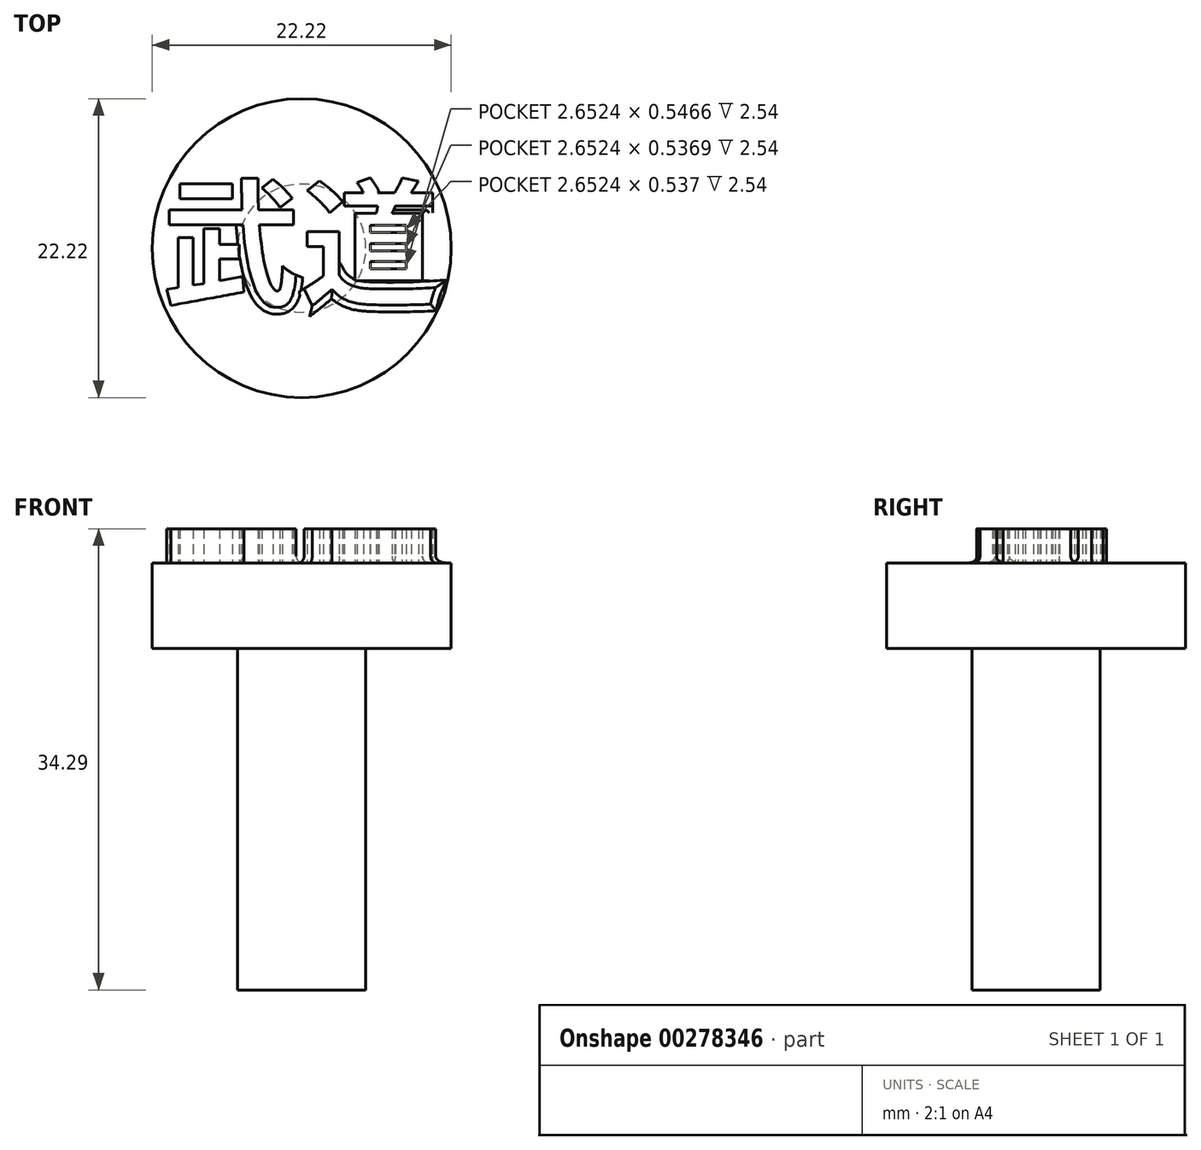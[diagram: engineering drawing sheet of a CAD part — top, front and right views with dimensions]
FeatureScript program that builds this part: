
annotation { "Feature Type Name" : "Feature", "Feature Type Description" : "" }
export const myFeature = defineFeature(function(context is Context, id is Id, definition is map)
    precondition{}
    {
        {
            var Q0;
            Q0=qCreatedBy(makeId("Top.planeOp"),FACE);
            var sketch = newSketch(context, id + "F0", { "sketchPlane" : qUnion([Q0])});
            skCircle(sketch, "E0", {"center": v(0, 0) * mm, "radius": 4.76 * mm});
            skSolve(sketch);
        }
        {
            var Q0;
            Q0 = qSketchRegion(id + "F0", true);
            extrude(context, id + "F1", {"entities" : qUnion([Q0]), "depth" : 25.4 * mm});
        }
        {
            var Q0;
            Q0=makeQuery(id+"F1.opExtrude","CAP_FACE",FACE,{"disambiguationData":[OSD([sQuery(id+"F0.wireOp",EDGE,"E0")])],"isStart":false});
            var sketch = newSketch(context, id + "F2", { "sketchPlane" : qUnion([Q0])});
            skCircle(sketch, "E1", {"center": v(0, 0) * mm, "radius": 11.11 * mm});
            skSolve(sketch);
        }
        {
            var Q0;
            Q0 = qSketchRegion(id + "F2", true);
            extrude(context, id + "F3", {"entities" : qUnion([Q0]), "operationType" : NewBodyOperationType.ADD, "depth" : 6.35 * mm});
        }
        {
            var Q0;
            Q0=makeQuery(id+"F3.opExtrude","CAP_FACE",FACE,{"disambiguationData":[OSD([sQuery(id+"F2.wireOp",EDGE,"E1")])],"isStart":false});
            var sketch = newSketch(context, id + "F4", { "sketchPlane" : qUnion([Q0])});
            skText(sketch, "E2", { "text": "武道", "fontName": "NotoSansCJKjp-Bold.otf"});
            const initialGuessF4  = {"E2": [-0.0104, -0.0035, 1, 0, 0.00743]};
            skSetInitialGuess(sketch, initialGuessF4);
            skSolve(sketch);
        }
        {
            var Q0;
            Q0 = qSketchRegion(id + "F4", true);
            extrude(context, id + "F5", {"entities" : qUnion([Q0]), "operationType" : NewBodyOperationType.ADD, "depth" : 2.54 * mm});
        }
        {
            var Q0;
            Q0=makeQuery(id+"F5.opExtrude","CAP_EDGE",EDGE,{"disambiguationData":[OSD([sQuery(id+"F4.wireOp",EDGE,"E2.sketch_text.stroke-32")])],"isStart":true});
            var Q1;
            Q1=makeQuery(id+"F5.opExtrude","CAP_EDGE",EDGE,{"disambiguationData":[OSD([sQuery(id+"F4.wireOp",EDGE,"E2.sketch_text.stroke-81")])],"isStart":true});
            var Q2;
            Q2=makeQuery(id+"F5.opExtrude","CAP_EDGE",EDGE,{"disambiguationData":[OSD([sQuery(id+"F4.wireOp",EDGE,"E2.sketch_text.stroke-80")])],"isStart":true});
            var Q3;
            Q3=makeQuery(id+"F5.opExtrude","CAP_EDGE",EDGE,{"disambiguationData":[OSD([sQuery(id+"F4.wireOp",EDGE,"E2.sketch_text.stroke-82")])],"isStart":true});
            var Q4;
            Q4=makeQuery(id+"F5.opExtrude","CAP_EDGE",EDGE,{"disambiguationData":[OSD([sQuery(id+"F4.wireOp",EDGE,"E2.sketch_text.stroke-83")])],"isStart":true});
            var Q5;
            Q5=makeQuery(id+"F5.opExtrude","CAP_EDGE",EDGE,{"disambiguationData":[OSD([sQuery(id+"F4.wireOp",EDGE,"E2.sketch_text.stroke-84")])],"isStart":true});
            var Q6;
            Q6=makeQuery(id+"F5.opExtrude","CAP_EDGE",EDGE,{"disambiguationData":[OSD([sQuery(id+"F4.wireOp",EDGE,"E2.sketch_text.stroke-85")])],"isStart":true});
            var Q7;
            Q7=makeQuery(id+"F5.opExtrude","CAP_EDGE",EDGE,{"disambiguationData":[OSD([sQuery(id+"F4.wireOp",EDGE,"E2.sketch_text.stroke-52")])],"isStart":true});
            var Q8;
            Q8=makeQuery(id+"F5.opExtrude","CAP_EDGE",EDGE,{"disambiguationData":[OSD([sQuery(id+"F4.wireOp",EDGE,"E2.sketch_text.stroke-55")])],"isStart":true});
            var Q9;
            Q9=makeQuery(id+"F5.opExtrude","CAP_EDGE",EDGE,{"disambiguationData":[OSD([sQuery(id+"F4.wireOp",EDGE,"E2.sketch_text.stroke-53")])],"isStart":true});
            fillet(context, id + "F6", {"entities" : qUnion([Q0, Q1, Q2, Q3, Q4, Q5, Q6, Q7, Q8, Q9]), "radius" : 0.5 * mm, "tangentPropagation" : true, "allowEdgeOverflow" : false});
        }
    });
